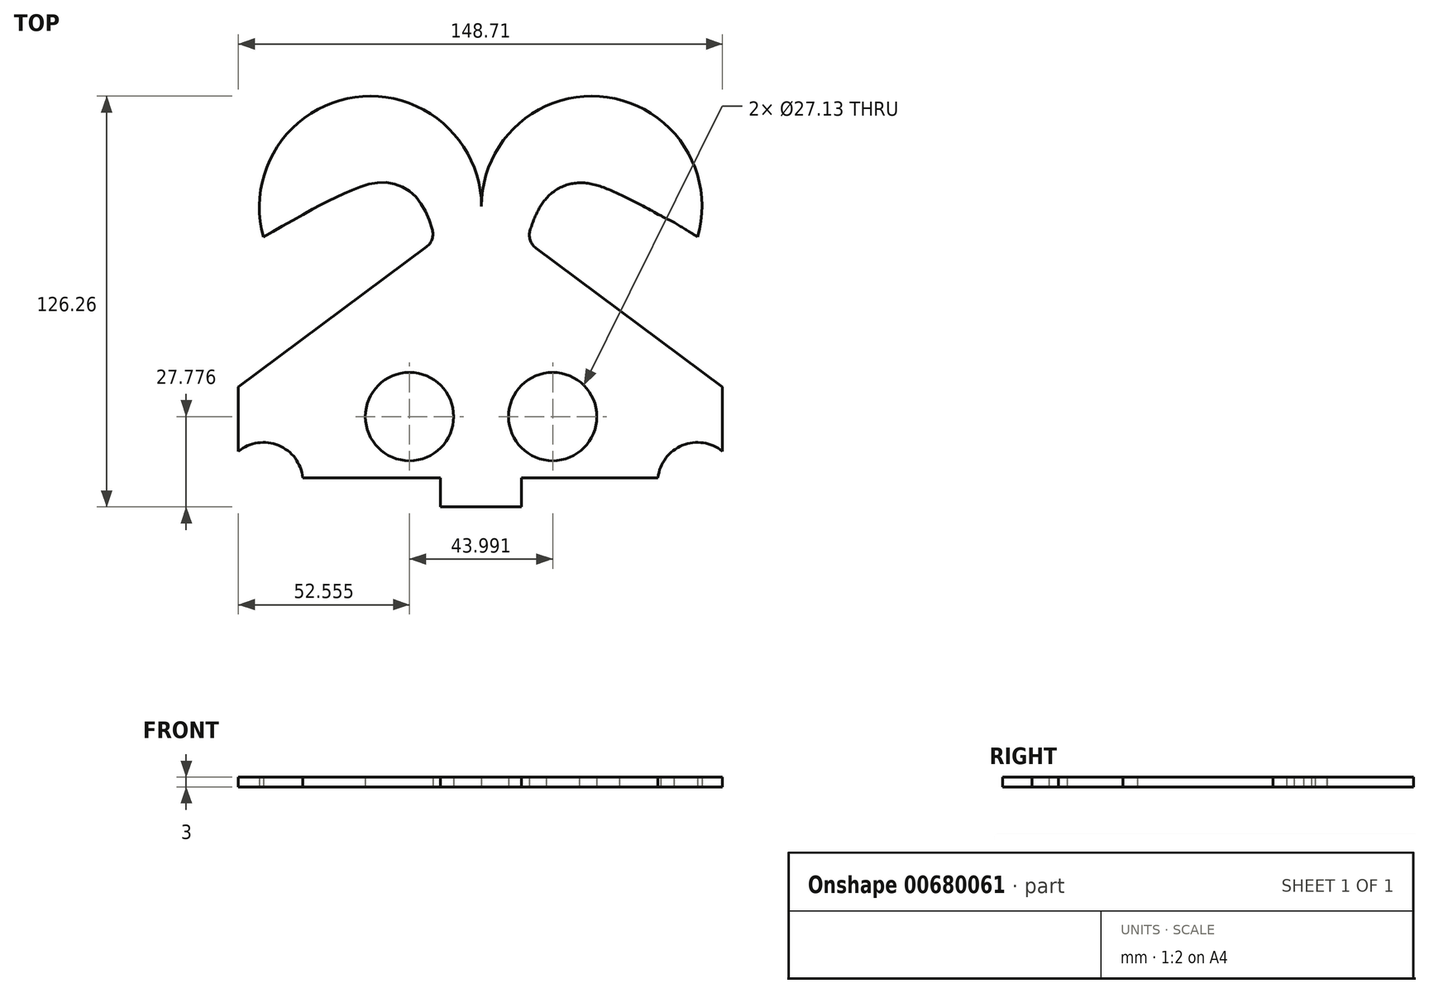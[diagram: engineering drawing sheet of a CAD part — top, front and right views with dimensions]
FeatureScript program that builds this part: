
annotation { "Feature Type Name" : "Feature", "Feature Type Description" : "" }
export const myFeature = defineFeature(function(context is Context, id is Id, definition is map)
    precondition{}
    {
        {
            var Q0;
            Q0=qCreatedBy(makeId("Top.planeOp"),FACE);
            var sketch = newSketch(context, id + "F0", { "sketchPlane" : qUnion([Q0])});
            skLineSegment(sketch, "E0", {"start": v(-16.81, 42.98) * mm, "end": v(-74.55, 0) * mm});
            skLineSegment(sketch, "E1", {"start": v(-74.55, 0) * mm, "end": v(-74.55, -19.8) * mm});
            skLineSegment(sketch, "E2", {"start": v(-54.75, -27.9) * mm, "end": v(0, -27.9) * mm});
            skLineSegment(sketch, "E3.MirrorCS", {"start": v(16.85, 42.67) * mm, "end": v(74.16, 0) * mm});
            skLineSegment(sketch, "E4.MirrorCS", {"start": v(54.36, -27.9) * mm, "end": v(-0.4, -27.9) * mm});
            skLineSegment(sketch, "E5.MirrorCS", {"start": v(74.16, 0) * mm, "end": v(74.16, -19.8) * mm});
            skArc(sketch, "E6", {"start": v(-54.75, -27.9) * mm, "mid": v(-62.25, -17.97) * mm, "end": v(-74.55, -19.8) * mm});
            skPoint(sketch, "E6.third.point", {"position": v(-77.85, -34.5) * mm});
            skPoint(sketch, "E7.MirrorP", {"position": v(77.46, -34.5) * mm});
            skArc(sketch, "E8.MirrorC", {"start": v(54.36, -27.9) * mm, "mid": v(61.85, -17.97) * mm, "end": v(74.16, -19.8) * mm});
            skLineSegment(sketch, "E9", {"start": v(0, -36.9) * mm, "end": v(-12.45, -36.9) * mm});
            skLineSegment(sketch, "E10", {"start": v(-12.45, -36.9) * mm, "end": v(-12.45, -27.9) * mm});
            skLineSegment(sketch, "E11.MirrorCS", {"start": v(12.45, -36.9) * mm, "end": v(12.45, -27.9) * mm});
            skLineSegment(sketch, "E12", {"start": v(0, -36.9) * mm, "end": v(12.45, -36.9) * mm});
            skPoint(sketch, "E13.start.orphan", {"position": v(0, 55.5) * mm});
            skLineSegment(sketch, "E14", {"start": v(0, 55.5) * mm, "end": v(0.14, 55.5) * mm});
            skArc(sketch, "E15", {"start": v(0.13, 55.5) * mm, "mid": v(-38.76, 89) * mm, "end": v(-66.88, 46.05) * mm});
            skArc(sketch, "E16", {"start": v(66.53, 46.1) * mm, "mid": v(38.75, 89.03) * mm, "end": v(0.14, 55.5) * mm});
            skPoint(sketch, "E17", {"position": v(-44.16, 22.63) * mm});
            skPoint(sketch, "E18", {"position": v(43.33, 22.95) * mm});
            skPoint(sketch, "E19", {"position": v(-66.88, 46.05) * mm});
            skPoint(sketch, "E20", {"position": v(66.52, 46.05) * mm});
            skPoint(sketch, "E21.start.orphan", {"position": v(34, 44.79) * mm});
            skFitSpline(sketch, "E22", {"points": [v(-14, 45.08) * mm, v(-19.7, 58.01) * mm, v(-29.9, 62.84) * mm, v(-42.25, 59.35) * mm, v(-54.87, 52.91) * mm, v(-66.88, 46.05) * mm, v(-59.17, 50.76) * mm], "startDerivative": vector(-23.96, 81.26) * mm, "endDerivative": vector(83.85, 50.75) * mm});
            skFitSpline(sketch, "E23.MirrorCS", {"points": [v(14.22, 45) * mm, v(20, 57.91) * mm, v(30.22, 62.7) * mm, v(42.55, 59.14) * mm, v(55.13, 52.63) * mm, v(67.1, 45.72) * mm, v(59.42, 50.47) * mm], "startDerivative": vector(24.37, 81.14) * mm, "endDerivative": vector(-83.6, 51.17) * mm});
            skPoint(sketch, "E24.start.orphan", {"position": v(-11.92, 0) * mm});
            skPoint(sketch, "E25.center.orphan", {"position": v(-27.5, 0) * mm});
            skArc(sketch, "E26.filletArc", {"start": v(-16.81, 42.98) * mm, "mid": v(-15.04, 45.46) * mm, "end": v(-15.04, 48.5) * mm});
            skFitSpline(sketch, "E27", {"points": [v(14, 44.79) * mm, v(20, 57.91) * mm, v(30.22, 62.7) * mm, v(42.55, 59.14) * mm, v(55.13, 52.63) * mm, v(59.42, 50.47) * mm], "startDerivative": vector(19.83, 64.63) * mm, "endDerivative": vector(28.07, -13.85) * mm});
            skArc(sketch, "E28.filletArc", {"start": v(15.09, 48.24) * mm, "mid": v(15.07, 45.17) * mm, "end": v(16.85, 42.67) * mm});
            skPoint(sketch, "E29.end.orphan", {"position": v(-11.92, -9.36) * mm});
            skLineSegment(sketch, "E30", {"start": v(0, -9.12) * mm, "end": v(-8.25, -9.12) * mm});
            skCircle(sketch, "E31", {"center": v(-22, -9.12) * mm, "radius": 13.57 * mm});
            skLineSegment(sketch, "E32.MirrorCS", {"start": v(0, -9.12) * mm, "end": v(8.25, -9.12) * mm});
            skCircle(sketch, "E33.MirrorC", {"center": v(22, -9.12) * mm, "radius": 13.57 * mm});
            skPoint(sketch, "E34.start.orphan", {"position": v(0, -2.66) * mm});
            skPoint(sketch, "E35.end.orphan", {"position": v(0, 0) * mm});
            skSolve(sketch);
        }
        {
            var Q0;
            Q0=makeQuery(id+"F0.imprint","IMPRINT",FACE,{"disambiguationData":[TD([[makeQuery(id+"F0.imprint","IMPRINT",EDGE,{"derivedFrom":sQuery(id+"F0.wireOp",EDGE,"E9")}),-1.0]])]});
            var Q1;
            {var subQ0=sQuery(id+"F0.wireOp",EDGE,"E22");var subQ1=sQuery(id+"F0.wireOp",EDGE,"E15");var subQ2=makeQuery(id+"F0.imprint","INTERSECT",VERTEX,{"disambiguationData":[OD(0.0)],"derivedFrom":[subQ1,subQ0]});Q1=makeQuery(id+"F0.imprint","IMPRINT",FACE,{"disambiguationData":[TD([[makeQuery(id+"F0.imprint","IMPRINT",EDGE,{"disambiguationData":[TD([[subQ2,1.0]])],"derivedFrom":subQ1}),-1.0]])]});}
            var Q2;
            Q2=makeQuery(id+"F0.imprint","IMPRINT",FACE,{"disambiguationData":[TD([[makeQuery(id+"F0.imprint","IMPRINT",EDGE,{"derivedFrom":sQuery(id+"F0.wireOp",EDGE,"E0")}),1.0]])]});
            extrude(context, id + "F1", {"entities" : qUnion([Q0, Q1, Q2]), "depth" : 3 * mm, "offsetDistance" : 25 * mm});
        }
    });
